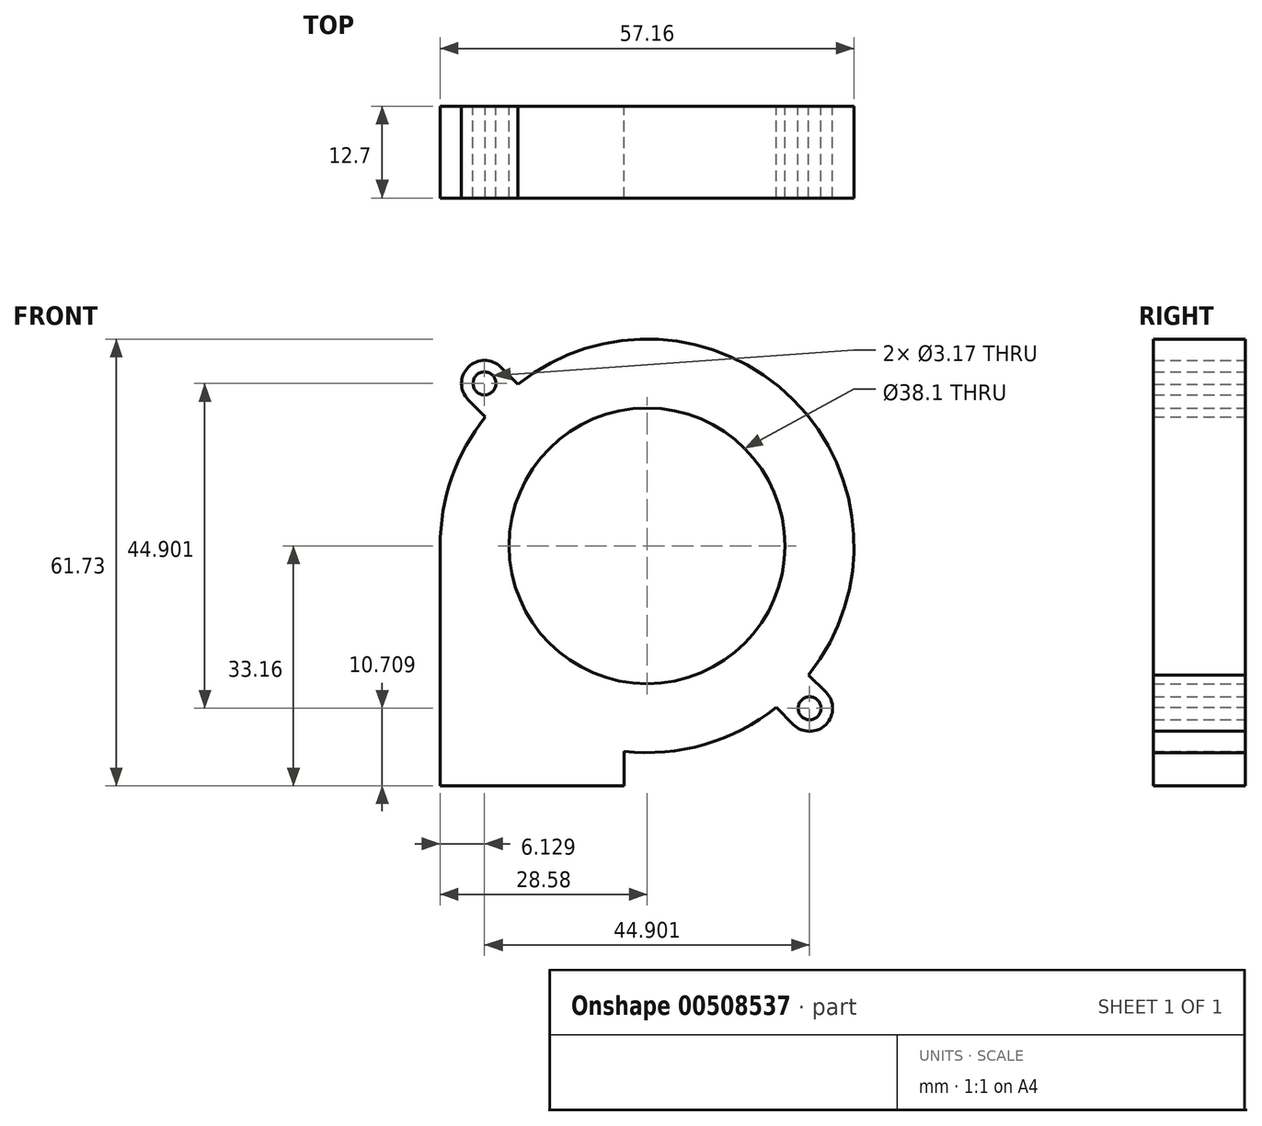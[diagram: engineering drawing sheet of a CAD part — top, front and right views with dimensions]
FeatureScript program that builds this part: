
annotation { "Feature Type Name" : "Feature", "Feature Type Description" : "" }
export const myFeature = defineFeature(function(context is Context, id is Id, definition is map)
    precondition{}
    {
        {
            var Q0;
            Q0=qCreatedBy(makeId("Front.planeOp"),FACE);
            var sketch = newSketch(context, id + "F0", { "sketchPlane" : qUnion([Q0])});
            skCircle(sketch, "E0", {"center": v(0, 0) * mm, "radius": 19.05 * mm});
            skArc(sketch, "E1", {"start": v(-3.17, -28.4) * mm, "mid": v(7.93, -27.45) * mm, "end": v(17.84, -22.33) * mm});
            skLineSegment(sketch, "E2", {"start": v(-28.58, 0) * mm, "end": v(-28.58, -33.16) * mm});
            skLineSegment(sketch, "E3", {"start": v(-28.57, -33.16) * mm, "end": v(-3.17, -33.16) * mm});
            skLineSegment(sketch, "E4", {"start": v(-3.17, -33.16) * mm, "end": v(-3.17, -28.4) * mm});
            skArc(sketch, "E5", {"start": v(20.2, -24.7) * mm, "mid": v(24.7, -24.7) * mm, "end": v(24.7, -20.2) * mm});
            skLineSegment(sketch, "E6", {"start": v(-37.67, 37.67) * mm, "end": v(39.28, -39.28) * mm, "construction": true});
            skLineSegment(sketch, "E7", {"start": v(17.84, -22.33) * mm, "end": v(20.2, -24.7) * mm});
            skLineSegment(sketch, "E8", {"start": v(22.33, -17.84) * mm, "end": v(24.7, -20.2) * mm});
            skArc(sketch, "E9.trimOffspring", {"start": v(22.33, -17.84) * mm, "mid": v(20.2, 20.2) * mm, "end": v(-17.84, 22.33) * mm});
            skCircle(sketch, "E10", {"center": v(22.45, -22.45) * mm, "radius": 1.59 * mm});
            skLineSegment(sketch, "E11", {"start": v(-37.25, -37.25) * mm, "end": v(42.05, 42.05) * mm, "construction": true});
            skArc(sketch, "E12.MirrorCS", {"start": v(-24.7, 20.2) * mm, "mid": v(-24.7, 24.7) * mm, "end": v(-20.2, 24.7) * mm});
            skCircle(sketch, "E13.MirrorC", {"center": v(-22.45, 22.45) * mm, "radius": 1.59 * mm});
            skLineSegment(sketch, "E14.MirrorCS", {"start": v(-17.84, 22.33) * mm, "end": v(-20.2, 24.7) * mm});
            skLineSegment(sketch, "E15.MirrorCS", {"start": v(-22.33, 17.84) * mm, "end": v(-24.7, 20.2) * mm});
            skArc(sketch, "E16.trimOffspring", {"start": v(-22.33, 17.84) * mm, "mid": v(-26.97, 9.45) * mm, "end": v(-28.58, 0) * mm});
            skSolve(sketch);
        }
        {
            var Q0;
            Q0 = qSketchRegion(id + "F0", true);
            extrude(context, id + "F1", {"entities" : qUnion([Q0]), "depth" : 12.7 * mm});
        }
    });
